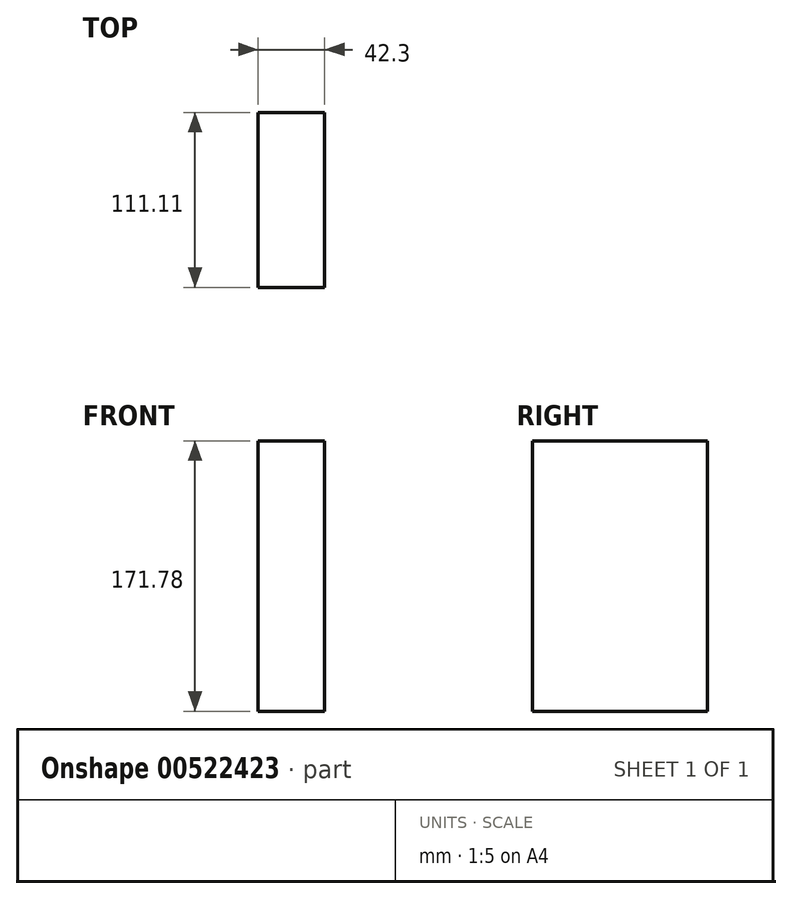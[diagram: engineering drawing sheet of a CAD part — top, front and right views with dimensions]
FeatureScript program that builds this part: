
annotation { "Feature Type Name" : "Feature", "Feature Type Description" : "" }
export const myFeature = defineFeature(function(context is Context, id is Id, definition is map)
    precondition{}
    {
        {
            var Q0;
            Q0=qCreatedBy(makeId("Top.planeOp"),FACE);
            var sketch = newSketch(context, id + "F0", { "sketchPlane" : qUnion([Q0])});
            skLineSegment(sketch, "E0.bottom", {"start": v(42.3, 111.11) * mm, "end": v(0, 111.11) * mm});
            skLineSegment(sketch, "E0.top", {"start": v(42.3, 0) * mm, "end": v(0, 0) * mm});
            skLineSegment(sketch, "E0.left", {"start": v(42.3, 111.11) * mm, "end": v(42.3, 0) * mm});
            skLineSegment(sketch, "E0.right", {"start": v(0, 111.11) * mm, "end": v(0, 0) * mm});
            skSolve(sketch);
        }
        {
            var Q0;
            Q0 = qSketchRegion(id + "F0", true);
            var sketch = newSketch(context, id + "F1", { "sketchPlane" : qUnion([Q0])});
            skSolve(sketch);
        }
        {
            var Q0;
            Q0=makeQuery(id+"F1.imprint","IMPRINT",FACE,{"disambiguationData":[TD([[makeQuery(id+"F1.imprint","IMPRINT",EDGE,{"derivedFrom":makeQuery(id+"F0.imprint","IMPRINT",EDGE,{"derivedFrom":sQuery(id+"F0.wireOp",EDGE,"E0.bottom")})}),1.0]])]});
            extrude(context, id + "F2", {"entities" : qUnion([Q0]), "depth" : 171.78 * mm, "offsetDistance" : 25.4 * mm});
        }
    });
